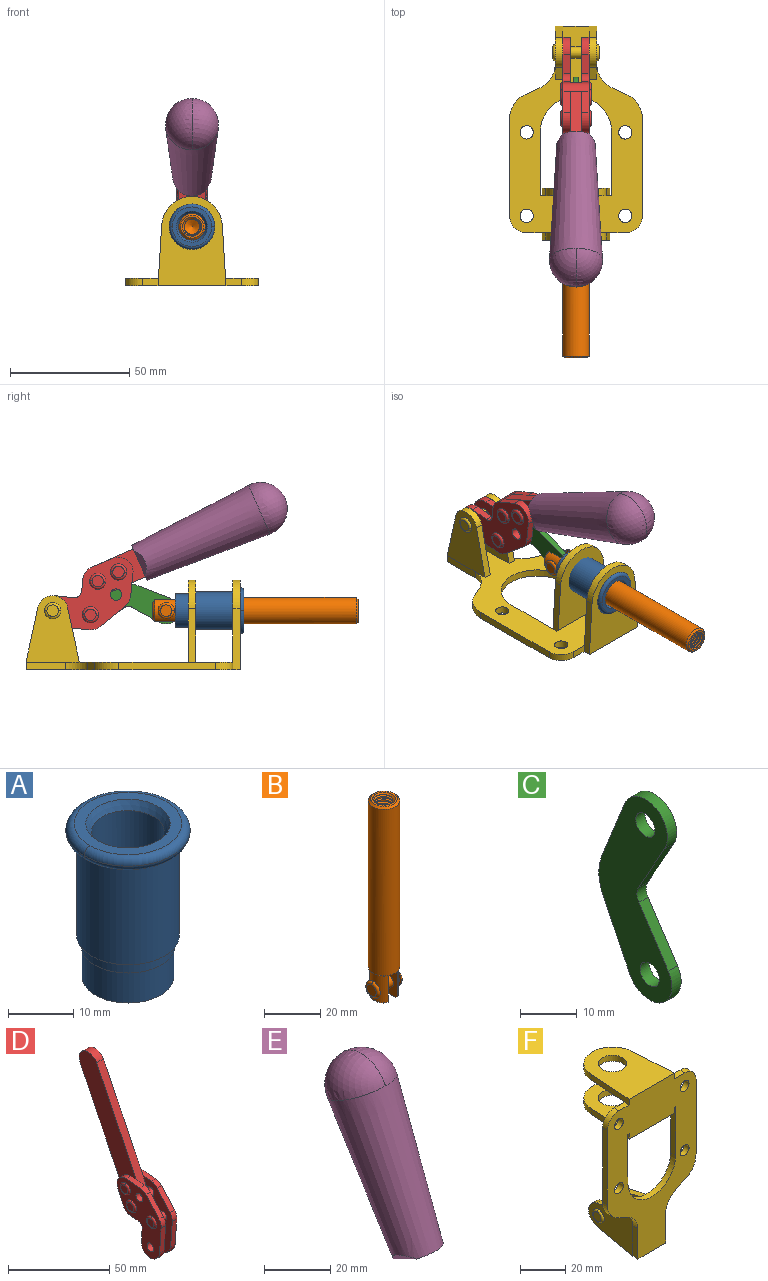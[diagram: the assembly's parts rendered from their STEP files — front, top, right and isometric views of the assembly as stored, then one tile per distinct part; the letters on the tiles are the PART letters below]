
ASSEMBLY  parts=6 mates=6
PART A: 15 faces, bbox 20.6x20.6x28.7 mm
  f0: torus R=8.26mm, axis (0,0,1), area 56.8mm2, adj f1,f10,f12
  f1: torus R=8.26mm, axis (0,0,1), area 56.8mm2, adj f0,f6,f13
  f2: cylinder r=5.59mm len=25.91mm, axis (0,0,1), area 909.6mm2, adj f3,f4
  f3: cone r=6.86mm half-angle=45deg, axis (0,0,-1), area 70.2mm2, adj f2,f14
  f4: cone r=6.47mm half-angle=30deg, axis (0,0,1), area 66.7mm2, adj f2,f13
  f5: cylinder r=7.04mm len=14.07mm, axis (0,0,1), area 252.6mm2, adj f11,f14
  f6: torus R=8.26mm, axis (0,0,1), area 56.8mm2, adj f1,f12,f13
  f7: cylinder r=7.16mm len=14.33mm, axis (0,0,1), area 91.5mm2, adj f9,f11
  f8: cylinder r=7.86mm len=18.42mm, axis (0,0,1), area 909.6mm2, adj f9,f10
  f9: plane 15.72x15.72mm, normal (0,0,-1), area 33mm2, adj f7,f8
  f10: plane 16.51x16.51mm, normal (0,0,-1), area 19.9mm2, adj f0,f8,f12
  f11: plane 14.33x14.33mm, normal (0,0,-1), area 5.7mm2, adj f5,f7
  f12: torus R=8.26mm, axis (0,0,1), area 56.8mm2, adj f0,f6,f10
  f13: plane 16.51x16.51mm, normal (0,0,1), area 82.7mm2, adj f1,f4,f6
  f14: plane 14.07x14.07mm, normal (0,0,-1), area 7.8mm2, adj f3,f5
PART B: 48 faces, bbox 12.6x11.1x86.1 mm
  f0: torus R=2.41mm, axis (-1,0,0), area 15mm2, adj f30,f32,f34
  f1: torus R=2.41mm, axis (-1,0,0), area 15mm2, adj f29,f31,f33
  f2: cylinder r=5.54mm len=72.39mm, axis (0,0,1), area 2518.5mm2, adj f3,f4,f42,f43
  f3: cone r=5.54mm half-angle=45deg, axis (0,0,1), area 7.6mm2, adj f2,f5,f41
  f4: cone r=5.54mm half-angle=45deg, axis (0,0,-1), area 34.9mm2, adj f2,f39
  f5: cylinder r=5.08mm len=11.48mm, axis (0,0,1), area 108.3mm2, adj f3,f7,f8,f41
  f6: cylinder r=2.41mm len=4.83mm, axis (-1,0,0), area 71.2mm2, adj f40,f41
  f7: cylinder r=2.41mm len=4.83mm, axis (-1,0,0), area 7.6mm2, adj f5,f34
  f8: cone r=5.08mm half-angle=45deg, axis (0,0,1), area 10.6mm2, adj f5,f37,f41
  f9: cone r=3.98mm half-angle=45deg, axis (0,0,1), area 17.6mm2, adj f27,f39,f45,f46,f47
  f10: cylinder r=2.41mm len=4.83mm, axis (-1,0,0), area 7.6mm2, adj f33,f38
  f11: cylinder r=3.2mm len=6.4mm, axis (0,0,1), area 78.4mm2, adj f12,f28,f44,f45,f47
  f12: cylinder r=3.2mm len=6.4mm, axis (0,0,1), area 10.5mm2, adj f11,f13,f45,f47
  f13: cylinder r=3.2mm len=6.4mm, axis (0,0,1), area 10.5mm2, adj f12,f14,f45,f47
  f14: cylinder r=3.2mm len=6.4mm, axis (0,0,1), area 10.5mm2, adj f13,f15,f45,f47
  f15: cylinder r=3.2mm len=6.4mm, axis (0,0,1), area 10.5mm2, adj f14,f16,f45,f47
  f16: cylinder r=3.2mm len=6.4mm, axis (0,0,1), area 10.5mm2, adj f15,f17,f45,f47
  f17: cylinder r=3.2mm len=6.4mm, axis (0,0,1), area 10.5mm2, adj f16,f18,f45,f47
  f18: cylinder r=3.2mm len=6.4mm, axis (0,0,1), area 10.5mm2, adj f17,f19,f45,f47
  f19: cylinder r=3.2mm len=6.4mm, axis (0,0,1), area 10.5mm2, adj f18,f20,f45,f47
  f20: cylinder r=3.2mm len=6.4mm, axis (0,0,1), area 10.5mm2, adj f19,f21,f45,f47
  f21: cylinder r=3.2mm len=6.4mm, axis (0,0,1), area 10.5mm2, adj f20,f22,f45,f47
  f22: cylinder r=3.2mm len=6.4mm, axis (0,0,1), area 10.5mm2, adj f21,f23,f45,f47
  f23: cylinder r=3.2mm len=6.4mm, axis (0,0,1), area 10.5mm2, adj f22,f24,f45,f47
  f24: cylinder r=3.2mm len=6.4mm, axis (0,0,1), area 10.5mm2, adj f23,f25,f45,f47
  f25: cylinder r=3.2mm len=6.4mm, axis (0,0,1), area 10.5mm2, adj f24,f26,f45,f47
  f26: cylinder r=3.2mm len=6.4mm, axis (0,0,1), area 10.5mm2, adj f25,f27,f45,f47
  f27: cylinder r=3.2mm len=6.4mm, axis (0,0,1), area 7.4mm2, adj f9,f26,f45,f47
  f28: cone r=3.2mm half-angle=60deg, axis (0,0,1), area 37.2mm2, adj f11
  f29: plane 4.83x4.83mm, normal (-1,0,0), area 18.3mm2, adj f1,f31
  f30: plane 4.83x4.83mm, normal (1,0,0), area 18.3mm2, adj f0,f32
  f31: torus R=2.41mm, axis (-1,0,0), area 15mm2, adj f1,f29,f33
  f32: torus R=2.41mm, axis (-1,0,0), area 15mm2, adj f0,f30,f34
  f33: plane 6.83x6.83mm, normal (1,0,0), area 18.3mm2, adj f1,f10,f31
  f34: plane 6.83x6.83mm, normal (-1,0,0), area 18.3mm2, adj f0,f7,f32
  f35: cone r=5.08mm half-angle=45deg, axis (0,0,1), area 10.6mm2, adj f36,f38,f40
  f36: plane 7.25x1.97mm, normal (0,0,-1), area 10mm2, adj f35,f40
  f37: plane 7.25x1.97mm, normal (0,0,-1), area 10mm2, adj f8,f41
  f38: cylinder r=5.08mm len=11.48mm, axis (0,0,1), area 108.3mm2, adj f10,f35,f40,f42
  f39: plane 9.55x9.55mm, normal (0,0,1), area 22mm2, adj f4,f9
  f40: plane 12.76x10.09mm, normal (1,0,0), area 95.7mm2, adj f6,f35,f36,f38,f42,f43
  f41: plane 12.76x10.09mm, normal (-1,0,0), area 95.7mm2, adj f3,f5,f6,f8,f37,f43
  f42: cone r=5.54mm half-angle=45deg, axis (0,0,1), area 7.6mm2, adj f2,f38,f40
  f43: plane 11.07x4.7mm, normal (0,0,-1), area 50.4mm2, adj f2,f40,f41
  f44: plane 0.89x0.62mm, normal (-1,0,0), area 0.3mm2, adj f11,f45,f46,f47
  f45: bspline ~24.8x7.63mm, area 266.6mm2, adj f9,f11,f12,f13,f14,f15,f16,f17
  f46: bspline ~24.87x7.63mm, area 73.6mm2, adj f9,f44,f45,f47
  f47: bspline ~24.98x7.63mm, area 272.5mm2, adj f9,f11,f12,f13,f14,f15,f16,f17
PART C: 12 faces, bbox 2.3x18.2x42.8 mm
  f0: cylinder r=2.4mm len=4.8mm, axis (1,0,0), area 34.9mm2, adj f4,f11
  f1: cylinder r=10.41mm len=8.47mm, axis (1,0,0), area 20.2mm2, adj f4,f9,f10,f11
  f2: cylinder r=3.05mm len=3.16mm, axis (1,0,0), area 7.7mm2, adj f4,f6,f7,f11
  f3: cylinder r=2.4mm len=4.8mm, axis (1,0,0), area 34.9mm2, adj f4,f11
  f4: plane 42.81x18.23mm, normal (-1,0,0), area 414.1mm2, adj f0,f1,f2,f3,f5,f6,f7,f8
  f5: cylinder r=5.54mm len=10.67mm, axis (1,0,0), area 41.8mm2, adj f4,f6,f10,f11
  f6: plane 11.66x6.53mm, normal (0,-0.87,-0.49), area 30.9mm2, adj f2,f4,f5,f11
  f7: plane 11.17x7.33mm, normal (0,-0.84,0.55), area 30.9mm2, adj f2,f4,f8,f11
  f8: cylinder r=5.54mm len=10.51mm, axis (1,0,0), area 41.8mm2, adj f4,f7,f9,f11
  f9: plane 13.67x6.67mm, normal (0,0.9,-0.44), area 35.1mm2, adj f1,f4,f8,f11
  f10: plane 14.1x5.7mm, normal (0,0.93,0.37), area 35.1mm2, adj f1,f4,f5,f11
  f11: plane 42.81x18.23mm, normal (1,0,0), area 414.1mm2, adj f0,f1,f2,f3,f5,f6,f7,f8
PART D: 59 faces, bbox 12.9x60.2x99.6 mm
  f0: torus R=2.39mm, axis (-1,0,0), area 14.9mm2, adj f20,f43,f51
  f1: torus R=2.39mm, axis (-1,0,0), area 14.9mm2, adj f19,f42,f51
  f2: torus R=2.39mm, axis (-1,0,0), area 14.9mm2, adj f18,f35,f51
  f3: torus R=2.39mm, axis (-1,0,0), area 14.9mm2, adj f14,f17,f23
  f4: torus R=2.39mm, axis (-1,0,0), area 14.9mm2, adj f13,f16,f23
  f5: torus R=2.39mm, axis (-1,0,0), area 14.9mm2, adj f12,f15,f23
  f6: cylinder r=2.39mm len=4.78mm, axis (1,0,0), area 46.5mm2, adj f48,f50,f51
  f7: cylinder r=2.39mm len=4.78mm, axis (1,0,0), area 46.5mm2, adj f50,f51
  f8: cylinder r=6.35mm len=12.68mm, axis (1,0,0), area 61.8mm2, adj f38,f39,f50,f51
  f9: cylinder r=2.39mm len=4.78mm, axis (-1,0,0), area 70.5mm2, adj f46,f50
  f10: cylinder r=2.39mm len=4.78mm, axis (-1,0,0), area 46.5mm2, adj f23,f45,f46
  f11: cylinder r=2.39mm len=4.78mm, axis (-1,0,0), area 46.5mm2, adj f23,f46
  f12: plane 4.78x4.78mm, normal (1,0,0), area 17.9mm2, adj f5,f15
  f13: plane 4.78x4.78mm, normal (1,0,0), area 17.9mm2, adj f4,f16
  f14: plane 4.78x4.78mm, normal (1,0,0), area 17.9mm2, adj f3,f17
  f15: torus R=2.39mm, axis (-1,0,0), area 14.9mm2, adj f5,f12,f23
  f16: torus R=2.39mm, axis (-1,0,0), area 14.9mm2, adj f4,f13,f23
  f17: torus R=2.39mm, axis (-1,0,0), area 14.9mm2, adj f3,f14,f23
  f18: plane 4.78x4.78mm, normal (-1,0,0), area 17.9mm2, adj f2,f35
  f19: plane 4.78x4.78mm, normal (-1,0,0), area 17.9mm2, adj f1,f42
  f20: plane 4.78x4.78mm, normal (-1,0,0), area 17.9mm2, adj f0,f43
  f21: plane 2.26x0.2mm, normal (1,0,0), area 0.2mm2, adj f31,f44
  f22: plane 2.26x0.2mm, normal (-1,0,0), area 0.2mm2, adj f41,f44
  f23: plane 39.37x30.77mm, normal (1,0,0), area 565.5mm2, adj f3,f4,f5,f10,f11,f15,f16,f17
  f24: cylinder r=6.1mm len=4.15mm, axis (-1,0,0), area 14.7mm2, adj f23,f25,f32,f46
  f25: plane 10.25x9.01mm, normal (0,-0.75,0.66), area 42.3mm2, adj f23,f24,f26,f46
  f26: cylinder r=6.35mm len=4.64mm, axis (-1,0,0), area 15.6mm2, adj f23,f25,f27,f46
  f27: plane 15.84x3.1mm, normal (0,-1,-0.07), area 49.2mm2, adj f23,f26,f28,f46
  f28: cylinder r=6.35mm len=12.68mm, axis (-1,0,0), area 61.8mm2, adj f23,f27,f29,f46
  f29: plane 8.11x3.1mm, normal (0,1,0.07), area 25.2mm2, adj f23,f28,f30,f46
  f30: cylinder r=3.05mm len=3.25mm, axis (-1,0,0), area 14.8mm2, adj f23,f29,f31,f46
  f31: plane 5.99x3.1mm, normal (0,0.07,-1), area 18.6mm2, adj f21,f23,f30,f44,f46
  f32: plane 9.5x3.1mm, normal (0,-0.07,1), area 29.5mm2, adj f23,f24,f33,f46,f47
  f33: cylinder r=6.1mm len=8.63mm, axis (-1,0,0), area 39.1mm2, adj f23,f32,f34,f47
  f34: plane 8.65x3.96mm, normal (0,0.91,-0.42), area 29.5mm2, adj f23,f33,f44,f47
  f35: torus R=2.39mm, axis (-1,0,0), area 14.9mm2, adj f2,f18,f51
  f36: plane 10.25x9.01mm, normal (0,-0.75,0.66), area 42.3mm2, adj f37,f49,f50,f51
  f37: cylinder r=6.35mm len=4.64mm, axis (1,0,0), area 15.6mm2, adj f36,f38,f50,f51
  f38: plane 15.84x3.1mm, normal (0,-1,-0.07), area 49.2mm2, adj f8,f37,f50,f51
  f39: plane 8.11x3.1mm, normal (0,1,0.07), area 25.2mm2, adj f8,f40,f50,f51
  f40: cylinder r=3.05mm len=3.25mm, axis (1,0,0), area 14.8mm2, adj f39,f41,f50,f51
  f41: plane 5.99x3.1mm, normal (0,0.07,-1), area 18.6mm2, adj f22,f40,f44,f50,f51
  f42: torus R=2.39mm, axis (-1,0,0), area 14.9mm2, adj f1,f19,f51
  f43: torus R=2.39mm, axis (-1,0,0), area 14.9mm2, adj f0,f20,f51
  f44: cylinder r=6.35mm len=12.12mm, axis (-1,0,0), area 128.9mm2, adj f21,f22,f23,f31,f34,f41,f46,f47
  f45: plane 2.65x1.35mm, normal (1,0,0), area 1mm2, adj f10,f55
  f46: plane 39.08x20.42mm, normal (-1,0,0), area 412.5mm2, adj f9,f10,f11,f24,f25,f26,f27,f28
  f47: plane 77.62x39.82mm, normal (1,0,0), area 850mm2, adj f32,f33,f34,f44,f53,f54,f55
  f48: plane 2.65x1.35mm, normal (-1,0,0), area 1mm2, adj f6,f55
  f49: cylinder r=6.1mm len=4.15mm, axis (1,0,0), area 14.7mm2, adj f36,f50,f51,f56
  f50: plane 39.08x20.42mm, normal (1,0,0), area 412.5mm2, adj f6,f7,f8,f9,f36,f37,f38,f39
  f51: plane 39.37x30.77mm, normal (-1,0,0), area 565.5mm2, adj f0,f1,f2,f6,f7,f8,f35,f36
  f52: plane 8.65x3.96mm, normal (0,0.91,-0.42), area 29.5mm2, adj f44,f51,f57,f58
  f53: plane 68.49x33.4mm, normal (0,0.9,-0.44), area 358.1mm2, adj f44,f47,f54,f58
  f54: cylinder r=6.35mm len=12.06mm, axis (1,0,0), area 93.7mm2, adj f47,f53,f55,f58
  f55: plane 68.49x33.4mm, normal (0,-0.9,0.44), area 358.1mm2, adj f44,f45,f46,f47,f48,f50,f54,f58
  f56: plane 9.5x3.1mm, normal (0,-0.07,1), area 29.5mm2, adj f49,f50,f51,f57,f58
  f57: cylinder r=6.1mm len=8.63mm, axis (1,0,0), area 39.1mm2, adj f51,f52,f56,f58
  f58: plane 77.62x39.82mm, normal (-1,0,0), area 850mm2, adj f44,f52,f53,f54,f55,f56,f57
PART E: 11 faces, bbox 22.3x42.6x64.5 mm
  f0: sphere r=11.13mm, area 411.4mm2, adj f1,f8
  f1: cone r=11.11mm half-angle=3.3deg, axis (0,0.44,0.9), area 3251.8mm2, adj f0,f7,f8,f9,f10
  f2: cylinder r=6.16mm len=11.7mm, axis (1,0,0), area 89.5mm2, adj f3,f4,f5,f6
  f3: plane 60.23x36.75mm, normal (-1,0,0), area 763.6mm2, adj f2,f4,f6,f10
  f4: plane 51.37x25.05mm, normal (0,0.9,-0.44), area 264.2mm2, adj f2,f3,f5,f10
  f5: plane 60.23x36.75mm, normal (1,0,0), area 763.6mm2, adj f2,f4,f6,f10
  f6: plane 51.37x25.05mm, normal (0,-0.9,0.44), area 264.2mm2, adj f2,f3,f5,f10
  f7: plane 9.95x5.95mm, normal (0.71,-0.31,-0.64), area 25.8mm2, adj f1,f10
  f8: sphere r=11.13mm, area 411.4mm2, adj f0,f1
  f9: plane 9.95x5.95mm, normal (-0.71,-0.31,-0.64), area 25.8mm2, adj f1,f10
  f10: plane 14.27x11.38mm, normal (0,-0.44,-0.9), area 106.7mm2, adj f1,f3,f4,f5,f6,f7,f9
PART F: 55 faces, bbox 55.7x37.4x89.8 mm
  f0: torus R=2.41mm, axis (-1,0,0), area 15mm2, adj f11,f15,f25
  f1: torus R=2.41mm, axis (-1,0,0), area 15mm2, adj f10,f12,f22
  f2: cylinder r=2.78mm len=5.56mm, axis (0,-1,0), area 54.2mm2, adj f30,f54
  f3: cylinder r=14.99mm len=29.97mm, axis (0,-1,0), area 145.9mm2, adj f30,f49,f53,f54
  f4: cylinder r=2.78mm len=5.56mm, axis (0,-1,0), area 54.2mm2, adj f30,f54
  f5: cylinder r=2.78mm len=5.56mm, axis (0,-1,0), area 54.2mm2, adj f30,f54
  f6: cylinder r=2.78mm len=5.56mm, axis (0,-1,0), area 54.2mm2, adj f30,f54
  f7: cylinder r=6.35mm len=12.7mm, axis (0,0,1), area 123.6mm2, adj f27,f51
  f8: cylinder r=6.35mm len=12.7mm, axis (0,0,-1), area 124.7mm2, adj f21,f35
  f9: cylinder r=2.41mm len=11.18mm, axis (-1,0,0), area 169.4mm2, adj f16,f19
  f10: plane 4.83x4.83mm, normal (1,0,0), area 18.3mm2, adj f1,f12
  f11: plane 4.83x4.83mm, normal (-1,0,0), area 18.3mm2, adj f0,f15
  f12: torus R=2.41mm, axis (-1,0,0), area 15mm2, adj f1,f10,f22
  f13: cylinder r=6.35mm len=12.41mm, axis (1,0,0), area 53.4mm2, adj f18,f19,f22,f23
  f14: cylinder r=6.35mm len=12.41mm, axis (-1,0,0), area 53.4mm2, adj f16,f17,f24,f25
  f15: torus R=2.41mm, axis (-1,0,0), area 15mm2, adj f0,f11,f25
  f16: plane 27.86x22.35mm, normal (1,0,0), area 425.4mm2, adj f9,f14,f17,f24,f30
  f17: plane 22.86x4.97mm, normal (0,0.21,0.98), area 72.5mm2, adj f14,f16,f25,f30
  f18: plane 22.86x4.97mm, normal (0,0.21,0.98), area 72.5mm2, adj f13,f19,f22,f30
  f19: plane 27.86x22.35mm, normal (-1,0,0), area 425.4mm2, adj f9,f13,f18,f23,f30
  f20: cylinder r=12.7mm len=25.35mm, axis (0,0,-1), area 119.8mm2, adj f21,f34,f35,f36
  f21: plane 34.21x28.07mm, normal (0,0,-1), area 702.4mm2, adj f8,f20,f30,f34,f36
  f22: plane 27.96x22.45mm, normal (1,0,0), area 407.2mm2, adj f1,f12,f13,f18,f23,f30,f42,f43
  f23: plane 22.86x4.97mm, normal (0,0.21,-0.98), area 72.5mm2, adj f13,f19,f22,f44
  f24: plane 22.86x4.97mm, normal (0,0.21,-0.98), area 72.5mm2, adj f14,f16,f25,f44
  f25: plane 27.86x22.35mm, normal (-1,0,0), area 407.1mm2, adj f0,f14,f15,f17,f24,f30,f45,f46
  f26: plane 3.1x0.95mm, normal (0,0,-1), area 2.7mm2, adj f30,f49,f50,f54
  f27: plane 34.21x28.07mm, normal (0,0,1), area 702.4mm2, adj f7,f28,f30,f50,f52
  f28: cylinder r=12.7mm len=25.35mm, axis (0,0,1), area 118.8mm2, adj f27,f50,f51,f52
  f29: plane 3.1x0.95mm, normal (0,0,-1), area 2.7mm2, adj f30,f52,f53,f54
  f30: plane 86.54x55.63mm, normal (0,1,0), area 2362.9mm2, adj f2,f3,f4,f5,f6,f16,f17,f18
  f31: plane 40.56x3.1mm, normal (-1,0,0), area 125.7mm2, adj f30,f32,f48,f54
  f32: cylinder r=7.11mm len=7.11mm, axis (0,-1,0), area 34.6mm2, adj f30,f31,f33,f54
  f33: plane 6.67x3.1mm, normal (0,0,1), area 20.4mm2, adj f30,f32,f34,f54
  f34: plane 25.39x3.13mm, normal (-1,0.06,0), area 79.5mm2, adj f20,f21,f33,f35,f54
  f35: plane 37.31x28.45mm, normal (0,0,1), area 789.9mm2, adj f8,f20,f34,f36,f54
  f36: plane 25.39x3.13mm, normal (1,0.06,0), area 79.5mm2, adj f20,f21,f35,f37,f54
  f37: plane 6.67x3.1mm, normal (0,0,1), area 20.4mm2, adj f30,f36,f38,f54
  f38: cylinder r=7.11mm len=7.11mm, axis (0,-1,0), area 34.6mm2, adj f30,f37,f39,f54
  f39: plane 40.56x3.1mm, normal (1,0,0), area 125.7mm2, adj f30,f38,f40,f54
  f40: cylinder r=11.18mm len=10.16mm, axis (0,-1,0), area 39.5mm2, adj f30,f39,f41,f54
  f41: plane 6.09x3.1mm, normal (0.42,0,-0.91), area 20.8mm2, adj f30,f40,f42,f54
  f42: cylinder r=11.18mm len=9.41mm, axis (0,-1,0), area 37.2mm2, adj f22,f30,f41,f43,f54
  f43: plane 16.5x3.1mm, normal (1,0,0), area 51.1mm2, adj f22,f42,f44,f54
  f44: plane 17.37x3.1mm, normal (0,0,-1), area 53.8mm2, adj f23,f24,f30,f43,f45,f54
  f45: plane 16.5x3.1mm, normal (-1,0,0), area 51.1mm2, adj f25,f44,f46,f54
  f46: cylinder r=11.18mm len=9.41mm, axis (0,-1,0), area 37.2mm2, adj f25,f30,f45,f47,f54
  f47: plane 6.09x3.1mm, normal (-0.42,0,-0.91), area 20.8mm2, adj f30,f46,f48,f54
  f48: cylinder r=11.18mm len=10.16mm, axis (0,-1,0), area 39.5mm2, adj f30,f31,f47,f54
  f49: plane 26.54x3.1mm, normal (-1,0,0), area 82.3mm2, adj f3,f26,f30,f54
  f50: plane 25.39x3.1mm, normal (1,0.06,0), area 78.8mm2, adj f26,f27,f28,f51,f54
  f51: plane 37.31x28.45mm, normal (0,0,-1), area 789.9mm2, adj f7,f28,f50,f52,f54
  f52: plane 25.39x3.1mm, normal (-1,0.06,0), area 78.8mm2, adj f27,f28,f29,f51,f54
  f53: plane 26.54x3.1mm, normal (1,0,0), area 82.3mm2, adj f3,f29,f30,f54
  f54: plane 89.66x55.63mm, normal (0,-1,0), area 2678.5mm2, adj f2,f3,f4,f5,f6,f26,f29,f31
PLACE A rot(axis=(1,0,0),90deg) t=(0,10.16,0)mm
PLACE B rot(axis=(0,-0.71,0.71),180deg) t=(0,9.22,49.23)mm
PLACE C rot(axis=(1,0,0),89deg) t=(0,8.76,-0.28)mm
PLACE D rot(axis=(1,0,0),92.1deg) t=(0,10.06,-1.16)mm
PLACE E rot(axis=(1,0,0),92.1deg) t=(0,10.06,-1.16)mm
PLACE F rot(axis=(1,0,0),90deg) t=(0,9.14,0)mm fixed
MATE revolute C.f3 <-> D.f4  axis (1,0,0) through (0,25.45,22.92)mm
MATE fastened F.f7 <-> A.f2  axis (0,-1,0) through (0,-37.25,24.61)mm
MATE fastened E.f2 <-> D.f54  axis (1,0,0) through (0,-47.28,67.82)mm
MATE revolute D.f7 <-> F.f0  axis (1,0,0) through (0,41.23,24.61)mm
MATE revolute B.f6 <-> C.f5  axis (1,0,0) through (0,-6.26,24.61)mm
MATE slider B.f2 <-> F.f7  axis (0,-1,0) through (0,-49.56,24.61)mm
